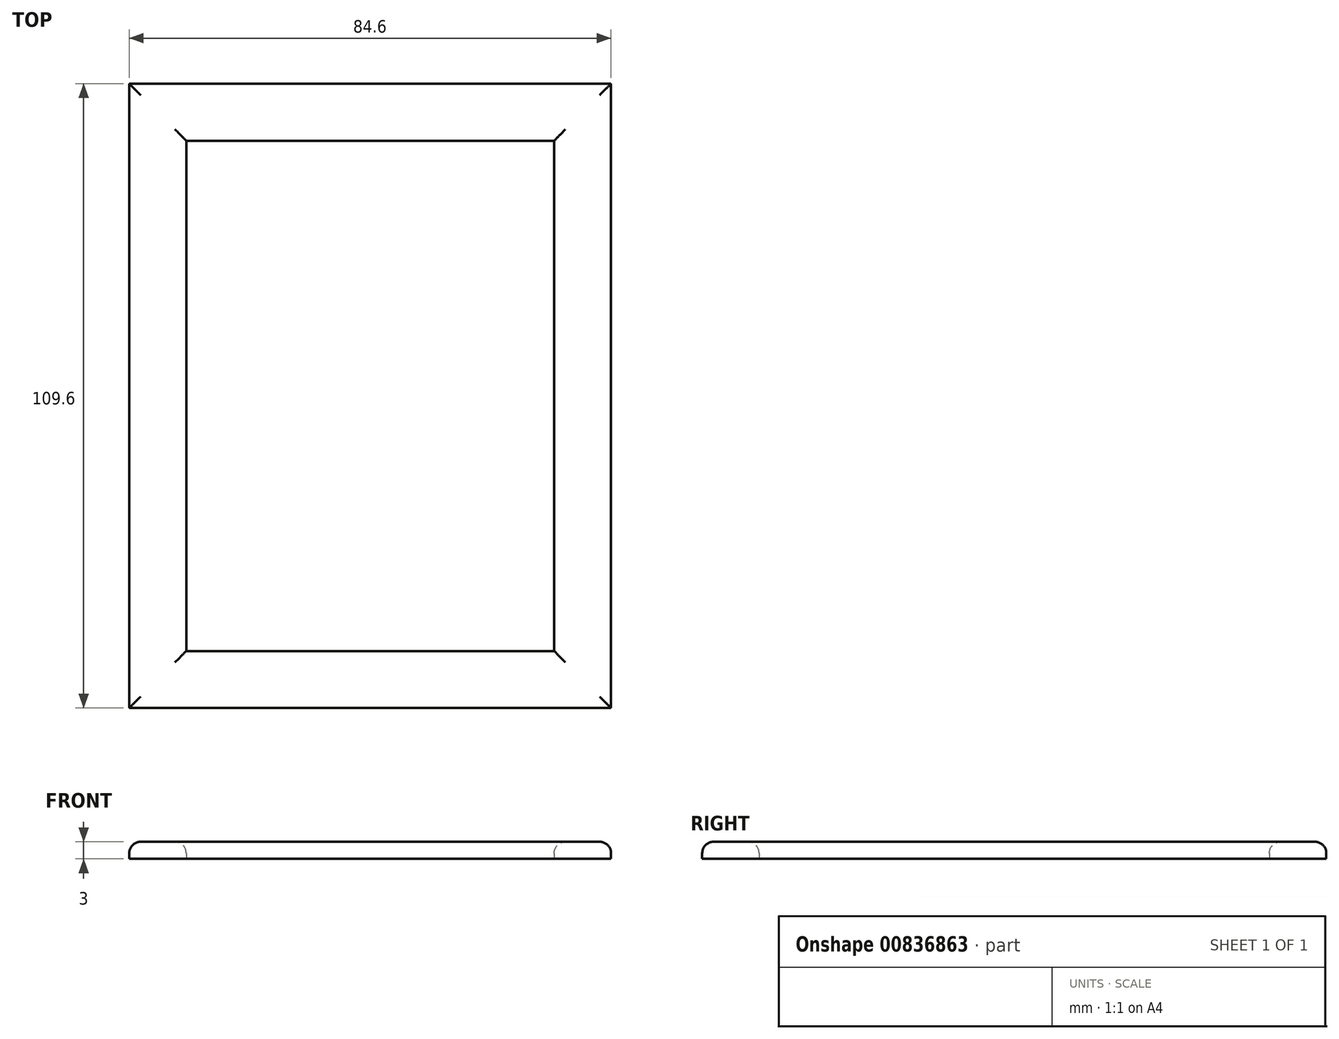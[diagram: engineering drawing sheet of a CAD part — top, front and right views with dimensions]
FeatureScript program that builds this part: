
annotation { "Feature Type Name" : "Feature", "Feature Type Description" : "" }
export const myFeature = defineFeature(function(context is Context, id is Id, definition is map)
    precondition{}
    {
        {
            var Q0;
            Q0=qCreatedBy(makeId("Top.planeOp"),FACE);
            var sketch = newSketch(context, id + "F0", { "sketchPlane" : qUnion([Q0])});
            skLineSegment(sketch, "E0.bottom", {"start": v(0, 0) * mm, "end": v(-64, 0) * mm});
            skLineSegment(sketch, "E0.top", {"start": v(0, 89) * mm, "end": v(-64, 89) * mm});
            skLineSegment(sketch, "E0.left", {"start": v(0, 0) * mm, "end": v(0, 89) * mm});
            skLineSegment(sketch, "E0.right", {"start": v(-64, 0) * mm, "end": v(-64, 89) * mm});
            skLineSegment(sketch, "E1.0", {"start": v(-64.3, -0.3) * mm, "end": v(-64.3, 89.3) * mm});
            skLineSegment(sketch, "E1.1", {"start": v(0.3, -0.3) * mm, "end": v(-64.3, -0.3) * mm});
            skLineSegment(sketch, "E1.2", {"start": v(0.3, -0.3) * mm, "end": v(0.3, 89.3) * mm});
            skLineSegment(sketch, "E1.3", {"start": v(0.3, 89.3) * mm, "end": v(-64.3, 89.3) * mm});
            skLineSegment(sketch, "E2.0", {"start": v(-74.3, -10.3) * mm, "end": v(-74.3, 99.3) * mm});
            skLineSegment(sketch, "E2.1", {"start": v(10.3, -10.3) * mm, "end": v(-74.3, -10.3) * mm});
            skLineSegment(sketch, "E2.2", {"start": v(10.3, -10.3) * mm, "end": v(10.3, 99.3) * mm});
            skLineSegment(sketch, "E2.3", {"start": v(10.3, 99.3) * mm, "end": v(-74.3, 99.3) * mm});
            skSolve(sketch);
        }
        {
            var Q0;
            Q0=makeQuery(id+"F0.imprint","IMPRINT",FACE,{"disambiguationData":[TD([[makeQuery(id+"F0.imprint","IMPRINT",EDGE,{"derivedFrom":sQuery(id+"F0.wireOp",EDGE,"E1.0")}),1.0]])]});
            extrude(context, id + "F1", {"entities" : qUnion([Q0]), "depth" : 3 * mm, "offsetDistance" : 25 * mm});
        }
        {
            var Q0;
            Q0=makeQuery(id+"F1.opExtrude","CAP_FACE",FACE,{"disambiguationData":[OSD([sQuery(id+"F0.wireOp",EDGE,"E1.0"),sQuery(id+"F0.wireOp",EDGE,"E1.1"),sQuery(id+"F0.wireOp",EDGE,"E1.2"),sQuery(id+"F0.wireOp",EDGE,"E1.3"),sQuery(id+"F0.wireOp",EDGE,"E2.0"),sQuery(id+"F0.wireOp",EDGE,"E2.1"),sQuery(id+"F0.wireOp",EDGE,"E2.2"),sQuery(id+"F0.wireOp",EDGE,"E2.3")])],"isStart":false});
            fillet(context, id + "F2", {"entities" : qUnion([Q0]), "radius" : 2 * mm, "tangentPropagation" : true, "allowEdgeOverflow" : false});
        }
    });
